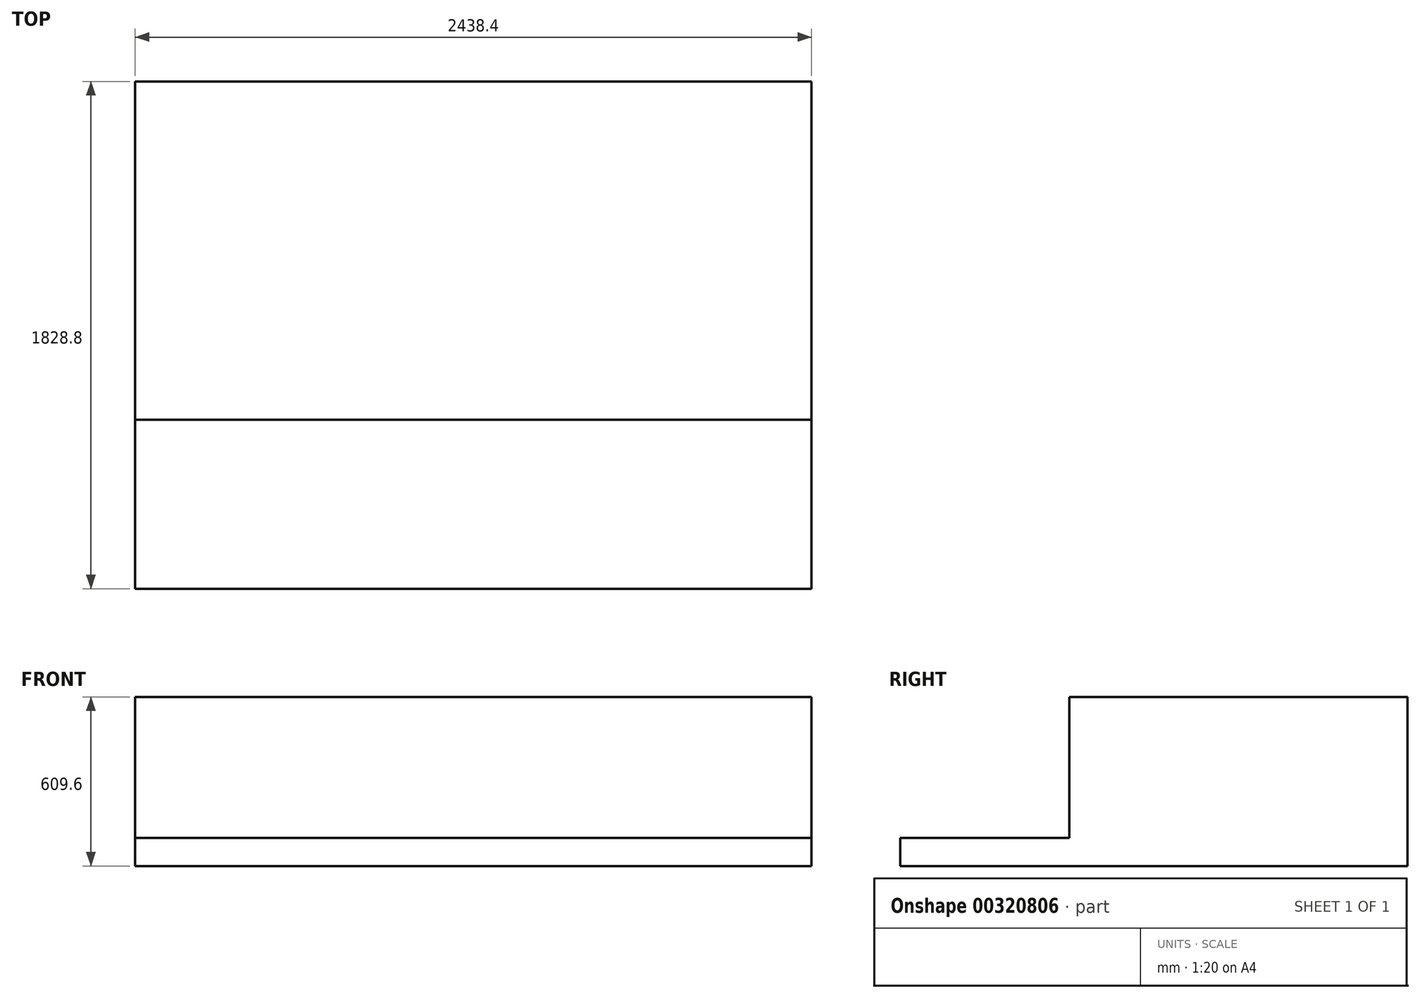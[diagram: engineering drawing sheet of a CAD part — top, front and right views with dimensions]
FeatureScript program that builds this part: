
annotation { "Feature Type Name" : "Feature", "Feature Type Description" : "" }
export const myFeature = defineFeature(function(context is Context, id is Id, definition is map)
    precondition{}
    {
        {
            var Q0;
            Q0=qCreatedBy(makeId("Right.planeOp"),FACE);
            var sketch = newSketch(context, id + "F0", { "sketchPlane" : qUnion([Q0])});
            skLineSegment(sketch, "E0", {"start": v(-914.4, 0) * mm, "end": v(914.4, 0) * mm});
            skLineSegment(sketch, "E1", {"start": v(-914.4, 0) * mm, "end": v(-914.4, 101.6) * mm});
            skLineSegment(sketch, "E2", {"start": v(-914.4, 101.6) * mm, "end": v(-304.8, 101.6) * mm});
            skLineSegment(sketch, "E3", {"start": v(-304.8, 101.6) * mm, "end": v(-304.8, 609.6) * mm});
            skLineSegment(sketch, "E4", {"start": v(-304.8, 609.6) * mm, "end": v(914.4, 609.6) * mm});
            skLineSegment(sketch, "E5", {"start": v(914.4, 609.6) * mm, "end": v(914.4, 0) * mm});
            skSolve(sketch);
        }
        {
            var Q0;
            Q0 = qSketchRegion(id + "F0", true);
            extrude(context, id + "F1", {"entities" : qUnion([Q0]), "endBound" : BoundingType.SYMMETRIC, "depth" : 2438.4 * mm});
        }
    });
